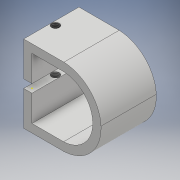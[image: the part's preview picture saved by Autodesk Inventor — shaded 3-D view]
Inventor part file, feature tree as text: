
AUTODESK INVENTOR PART (.ipt)
format: ipt  version: 2018.1 (Build 221171000, 171)  size: 148,992 bytes
history: native  units: mm
features: sketch x6, extrude x5, other x5
ambient origin geometry x8: Origin, YZ Plane, XZ Plane, XY Plane, X Axis, Y Axis, Z Axis, Center Point
bodies: Solide1 (feature_tree)
feature tree (16):
  extrude  "Extrusion1"  Depth=20.0mm TaperAngle=0.0deg
  extrude  "Extrusion2"  Depth=20.0mm TaperAngle=0.0deg
  sketch  "Esquisse3"
  sketch  "Esquisse4"
  other  "Plan de construction2"
  other  "Plan de construction3"
  extrude  "Extrusion6"  Depth=7.5mm TaperAngle=0.0deg
  extrude  "Extrusion7"  Depth=10.0mm
  extrude  "Extrusion9"  Depth=1.5mm
  other  "Filetage1"
  other  "Filetage2"
  other  "Filetage3"
  sketch  "Esquisse1"
  sketch  "Esquisse2"
  sketch  "Esquisse7"
  sketch  "Esquisse8"
